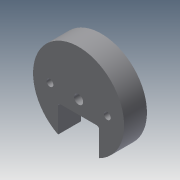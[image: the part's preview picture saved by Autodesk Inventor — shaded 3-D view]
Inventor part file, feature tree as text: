
AUTODESK INVENTOR PART (.ipt)
format: ipt  version: 2015 (Build 190159000, 159)  size: 143,360 bytes
history: native  units: mm
features: sketch x12, extrude x10, fillet x1
ambient origin geometry x8: Origin, YZ Plane, XZ Plane, XY Plane, X Axis, Y Axis, Z Axis, Center Point
bodies: Solid1 (feature_tree)
feature tree (23):
  extrude  "Extrusion1"  Depth=10.0mm TaperAngle=0.0deg
  extrude  "Extrusion2"  Depth=10.0mm TaperAngle=0.0deg
  extrude  "Extrusion3"  Depth=3.0mm
  sketch  "Sketch4"  dims[d9=10.0mm d10=0.0mm d11=10.0mm]
  sketch  "Sketch5"  dims[d12=10.0mm d13=0.0mm d14=6.0mm]
  extrude  "Extrusion4"  Depth=10.0mm
  extrude  "Extrusion5"  Depth=10.0mm
  extrude  "Extrusion6"  Depth=18.0mm
  extrude  "Extrusion7"  Depth=10.0mm TaperAngle=0.0deg
  extrude  "Extrusion8"  Depth=2.0mm
  extrude  "Extrusion9"  Depth=10.0mm TaperAngle=0.0deg
  extrude  "Extrusion10"  Depth=10.0mm
  fillet  "Fillet1"  Radius=10.0mm
  sketch  "Sketch1"  dims[d0=40.0mm d1=10.0mm d2=0.0mm]
  sketch  "Sketch2"  dims[d3=12.0mm d4=10.0mm d5=0.0mm]
  sketch  "Sketch3"  dims[d7=3.0mm d8=3.0mm]
  sketch  "Sketch6"  dims[d15=2.0mm d16=0.0mm d17=18.0mm]
  sketch  "Sketch7"  dims[d18=10.0mm d19=10.0mm d20=0.0mm]
  sketch  "Sketch8"  dims[d21=18.0mm d25=2.0mm]
  sketch  "Sketch9"  dims[d26=10.0mm d27=0.0mm d28=8.0mm d29=0.0mm]
  sketch  "Sketch10"  dims[d30=8.0mm d31=0.0mm d32=4.0mm d33=10.0mm d34=0.0mm]
  sketch  "Sketch11"  dims[d35=1.0mm]
  sketch  "Sketch12"
